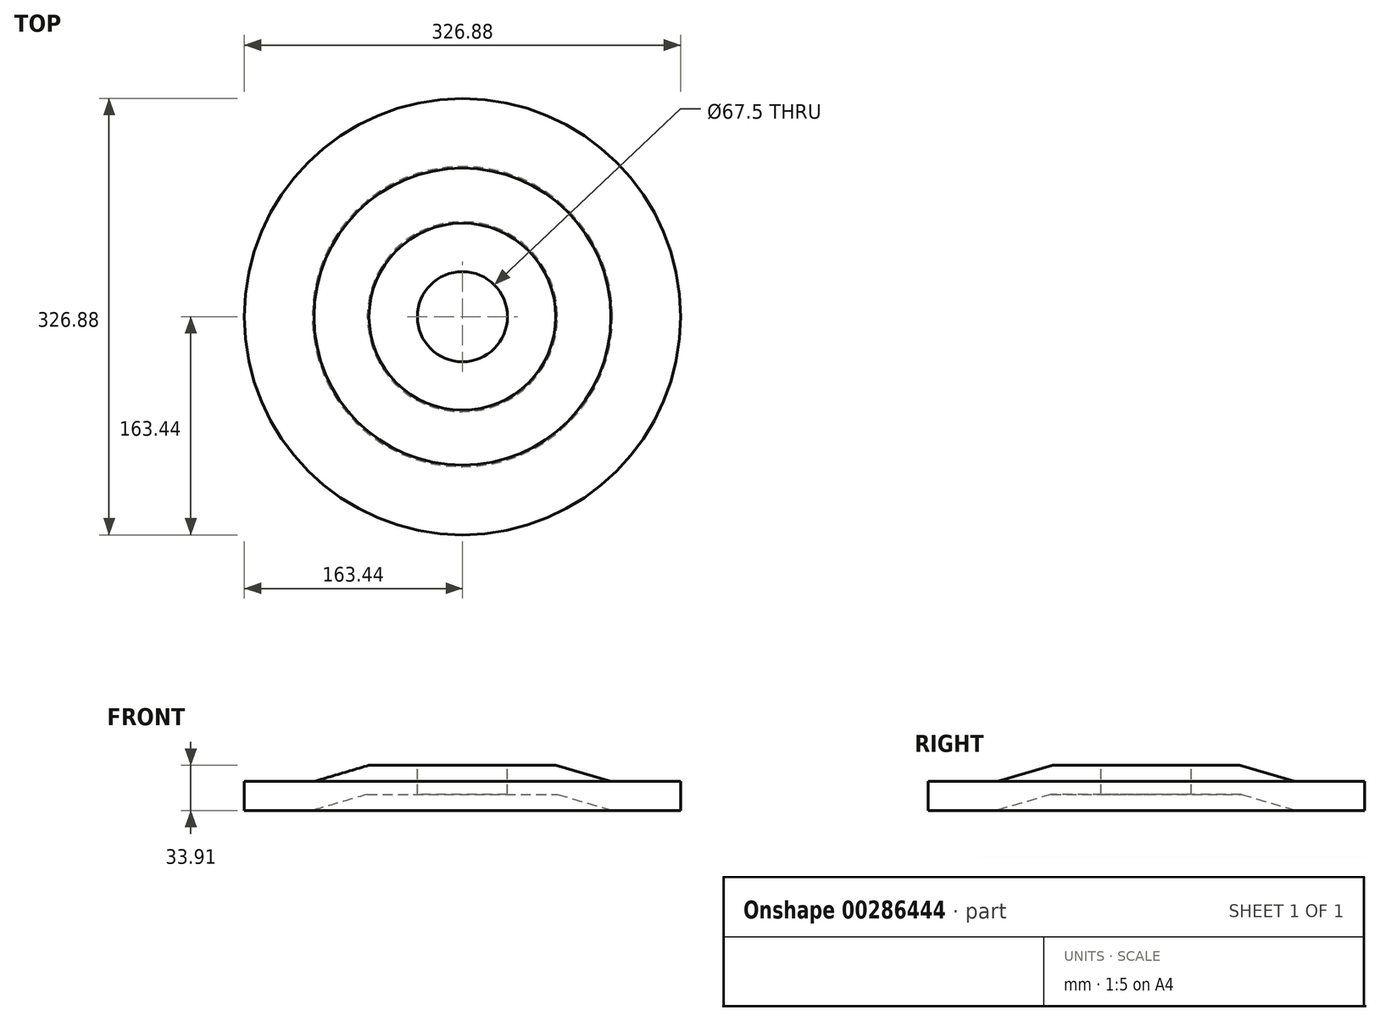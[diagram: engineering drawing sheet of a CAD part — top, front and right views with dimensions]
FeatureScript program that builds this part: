
annotation { "Feature Type Name" : "Feature", "Feature Type Description" : "" }
export const myFeature = defineFeature(function(context is Context, id is Id, definition is map)
    precondition{}
    {
        {
            var Q0;
            Q0=qCreatedBy(makeId("Right.planeOp"),FACE);
            var sketch = newSketch(context, id + "F0", { "sketchPlane" : qUnion([Q0])});
            skLineSegment(sketch, "E0", {"start": v(0, 33.9) * mm, "end": v(70, 33.9) * mm});
            skLineSegment(sketch, "E1", {"start": v(70, 33.9) * mm, "end": v(111.25, 21.72) * mm});
            skLineSegment(sketch, "E2", {"start": v(111.25, 21.72) * mm, "end": v(163.44, 21.72) * mm});
            skLineSegment(sketch, "E3", {"start": v(163.44, 21.72) * mm, "end": v(163.44, 0) * mm});
            skLineSegment(sketch, "E4", {"start": v(163.44, 0) * mm, "end": v(112.5, 0) * mm});
            skLineSegment(sketch, "E5", {"start": v(112.5, 0) * mm, "end": v(71.25, 12.03) * mm});
            skLineSegment(sketch, "E6", {"start": v(71.25, 12.03) * mm, "end": v(0, 12.03) * mm});
            skLineSegment(sketch, "E7", {"start": v(0, 12.03) * mm, "end": v(0, 33.9) * mm});
            skSolve(sketch);
        }
        {
            var Q0;
            Q0=makeQuery(id+"F0.imprint","IMPRINT",FACE,{"disambiguationData":[TD([[makeQuery(id+"F0.imprint","IMPRINT",EDGE,{"derivedFrom":sQuery(id+"F0.wireOp",EDGE,"E0")}),-1.0]])]});
            var Q1;
            Q1=sQuery(id+"F0.wireOp",EDGE,"E7");
            revolve(context, id + "F1", {"entities" : qUnion([Q0]), "axis" : qUnion([Q1]), "revolveType" : RevolveType.FULL});
        }
        {
            var Q0;
            Q0=makeQuery(id+"F1.opRevolve","SWEPT_FACE",FACE,{"disambiguationData":[OSD([sQuery(id+"F0.wireOp",EDGE,"E0")])]});
            var sketch = newSketch(context, id + "F2", { "sketchPlane" : qUnion([Q0])});
            skPoint(sketch, "E8", {"position": v(0, 0) * mm});
            skSolve(sketch);
        }
        {
            var Q0;
            Q0=sQuery(id+"F2.wireOp",VERTEX,"E8");
            var Q1;
            Q1=makeQuery(id+"F1.opRevolve","SWEPT_BODY",BODY,{"disambiguationData":[OSD([sQuery(id+"F0.wireOp",EDGE,"E0"),sQuery(id+"F0.wireOp",EDGE,"E1"),sQuery(id+"F0.wireOp",EDGE,"E2"),sQuery(id+"F0.wireOp",EDGE,"E3"),sQuery(id+"F0.wireOp",EDGE,"E4"),sQuery(id+"F0.wireOp",EDGE,"E5"),sQuery(id+"F0.wireOp",EDGE,"E6"),sQuery(id+"F0.wireOp",EDGE,"E7")])]});
            hole(context, id + "F3", {"style" : HoleStyle.SIMPLE, "endStyle" : HoleEndStyle.THROUGH, "holeDiameter" : (135 / 2) * mm, "tappedDepth" : 12 * mm, "tapClearance" : 3, "locations" : qUnion([Q0]), "scope" : qUnion([Q1])});
        }
    });
